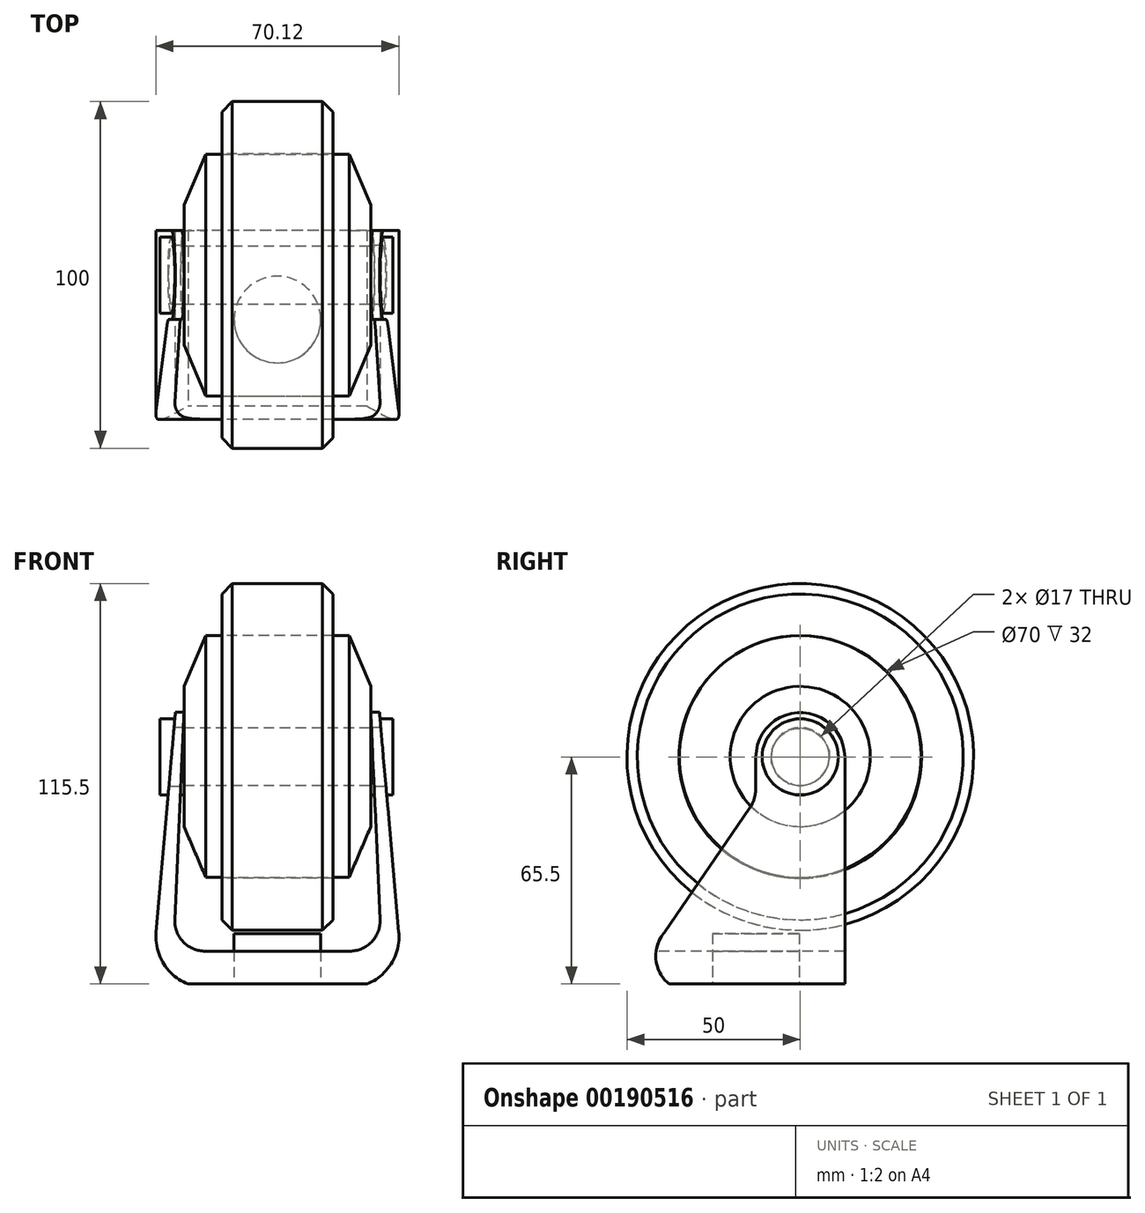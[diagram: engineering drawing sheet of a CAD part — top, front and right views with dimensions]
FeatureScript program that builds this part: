
annotation { "Feature Type Name" : "Feature", "Feature Type Description" : "" }
export const myFeature = defineFeature(function(context is Context, id is Id, definition is map)
    precondition{}
    {
        {
            var Q0;
            Q0=qCreatedBy(makeId("Top.planeOp"),FACE);
            var sketch = newSketch(context, id + "F0", { "sketchPlane" : qUnion([Q0])});
            skLineSegment(sketch, "E0.bottom", {"start": v(-35, 48) * mm, "end": v(35, 48) * mm});
            skLineSegment(sketch, "E0.top", {"start": v(-35, -48) * mm, "end": v(35, -48) * mm});
            skLineSegment(sketch, "E0.left", {"start": v(-35, 48) * mm, "end": v(-35, -48) * mm});
            skLineSegment(sketch, "E0.right", {"start": v(35, 48) * mm, "end": v(35, -48) * mm});
            skLineSegment(sketch, "E1", {"start": v(-35, 0) * mm, "end": v(35, 0) * mm, "construction": true});
            skLineSegment(sketch, "E2", {"start": v(0, 48) * mm, "end": v(0, -48) * mm, "construction": true});
            skLineSegment(sketch, "E3.bottom", {"start": v(-26.2, -41.35) * mm, "end": v(-17.8, -41.35) * mm});
            skLineSegment(sketch, "E3.top", {"start": v(-26.2, -31.65) * mm, "end": v(-17.8, -31.65) * mm});
            skLineSegment(sketch, "E3.left", {"start": v(-26.2, -41.35) * mm, "end": v(-26.2, -31.65) * mm});
            skLineSegment(sketch, "E3.right", {"start": v(-17.8, -41.35) * mm, "end": v(-17.8, -31.65) * mm});
            skPoint(sketch, "E4", {"position": v(-26.2, -36.5) * mm});
            skPoint(sketch, "E5", {"position": v(-22, -41.35) * mm});
            skLineSegment(sketch, "E6.MirrorCS", {"start": v(-26.2, 31.65) * mm, "end": v(-17.8, 31.65) * mm});
            skLineSegment(sketch, "E7.MirrorCS", {"start": v(-17.8, 41.35) * mm, "end": v(-17.8, 31.65) * mm});
            skPoint(sketch, "E8.MirrorP", {"position": v(-22, 41.35) * mm});
            skLineSegment(sketch, "E9.MirrorCS", {"start": v(-26.2, 41.35) * mm, "end": v(-17.8, 41.35) * mm});
            skLineSegment(sketch, "E10.MirrorCS", {"start": v(-26.2, 41.35) * mm, "end": v(-26.2, 31.65) * mm});
            skLineSegment(sketch, "E11.MirrorCS", {"start": v(17.8, 41.35) * mm, "end": v(17.8, 31.65) * mm});
            skLineSegment(sketch, "E12.MirrorCS", {"start": v(26.2, 31.65) * mm, "end": v(17.8, 31.65) * mm});
            skLineSegment(sketch, "E13.MirrorCS", {"start": v(26.2, 41.35) * mm, "end": v(26.2, 31.65) * mm});
            skLineSegment(sketch, "E14.MirrorCS", {"start": v(26.2, 41.35) * mm, "end": v(17.8, 41.35) * mm});
            skLineSegment(sketch, "E15.MirrorCS", {"start": v(26.2, -31.65) * mm, "end": v(17.8, -31.65) * mm});
            skLineSegment(sketch, "E16.MirrorCS", {"start": v(17.8, -41.35) * mm, "end": v(17.8, -31.65) * mm});
            skLineSegment(sketch, "E17.MirrorCS", {"start": v(26.2, -41.35) * mm, "end": v(17.8, -41.35) * mm});
            skLineSegment(sketch, "E18.MirrorCS", {"start": v(26.2, -41.35) * mm, "end": v(26.2, -31.65) * mm});
            skCircle(sketch, "E19", {"center": v(0, -41.35) * mm, "radius": 4.15 * mm});
            skCircle(sketch, "E20.MirrorC", {"center": v(0, 41.35) * mm, "radius": 4.15 * mm});
            skSolve(sketch);
        }
        {
            var Q0;
            Q0=makeQuery(id+"F0.imprint","IMPRINT",FACE,{"disambiguationData":[TD([[makeQuery(id+"F0.imprint","IMPRINT",EDGE,{"derivedFrom":sQuery(id+"F0.wireOp",EDGE,"E0.bottom")}),-1.0]])]});
            extrude(context, id + "F1", {"entities" : qUnion([Q0]), "depth" : 5 * mm});
        }
        {
            var Q0;
            Q0=qCreatedBy(makeId("Front.planeOp"),FACE);
            var sketch = newSketch(context, id + "F2", { "sketchPlane" : qUnion([Q0])});
            skLineSegment(sketch, "E21.0", {"start": v(-25, 5) * mm, "end": v(25, 5) * mm});
            skLineSegment(sketch, "E22.0.2", {"start": v(35, 5) * mm, "end": v(-35, 5) * mm, "construction": true});
            skLineSegment(sketch, "E23", {"start": v(0, 5) * mm, "end": v(0, 12) * mm});
            skLineSegment(sketch, "E24", {"start": v(0, 5) * mm, "end": v(-25, 5) * mm});
            skLineSegment(sketch, "E25", {"start": v(0, 12) * mm, "end": v(-25, 12) * mm});
            skArc(sketch, "E26", {"start": v(-25, 12) * mm, "mid": v(-25.8, 8.5) * mm, "end": v(-25, 5) * mm});
            skSolve(sketch);
        }
        {
            var Q0;
            Q0=makeQuery(id+"F2.imprint","IMPRINT",FACE,{"disambiguationData":[TD([[makeQuery(id+"F2.imprint","IMPRINT",EDGE,{"derivedFrom":sQuery(id+"F2.wireOp",EDGE,"E23")}),1.0]])]});
            var Q1;
            Q1=sQuery(id+"F2.wireOp",EDGE,"E23");
            revolve(context, id + "F3", {"operationType" : NewBodyOperationType.ADD, "entities" : qUnion([Q0]), "axis" : qUnion([Q1]), "revolveType" : RevolveType.FULL});
        }
        {
            var Q0;
            Q0=makeQuery(id+"F3.opRevolve","SWEPT_FACE",FACE,{"disambiguationData":[OSD([sQuery(id+"F2.wireOp",EDGE,"E25")])]});
            cPlane(context, id + "F4", {"entities" : qUnion([Q0]), "cplaneType" : CPlaneType.OFFSET, "offset" : 0 * mm, "width" : 150 * mm, "height" : 150 * mm});
        }
        {
            var Q0;
            Q0=qCreatedBy(id+"F4.planeOp",FACE);
            var sketch = newSketch(context, id + "F5", { "sketchPlane" : qUnion([Q0])});
            skCircle(sketch, "E27", {"center": v(0, 0) * mm, "radius": 12.5 * mm});
            skSolve(sketch);
        }
        {
            var Q0;
            Q0=makeQuery(id+"F5.imprint","IMPRINT",FACE,{"disambiguationData":[TD([[makeQuery(id+"F5.imprint","IMPRINT",EDGE,{"derivedFrom":sQuery(id+"F5.wireOp",EDGE,"E27")}),1.0]])]});
            extrude(context, id + "F6", {"entities" : qUnion([Q0]), "operationType" : NewBodyOperationType.ADD, "depth" : 15 * mm});
        }
        {
            var Q0;
            Q0=qCreatedBy(makeId("Front.planeOp"),FACE);
            cPlane(context, id + "F7", {"entities" : qUnion([Q0]), "cplaneType" : CPlaneType.OFFSET, "offset" : 27 * mm, "width" : 150 * mm, "height" : 150 * mm});
        }
        {
            var Q0;
            Q0=qCreatedBy(id+"F7.planeOp",FACE);
            var sketch = newSketch(context, id + "F8", { "sketchPlane" : qUnion([Q0])});
            skLineSegment(sketch, "E28", {"start": v(0, 12.5) * mm, "end": v(25.8, 12.5) * mm});
            skLineSegment(sketch, "E29", {"start": v(35, 27.44) * mm, "end": v(29.43, 90.85) * mm});
            skLineSegment(sketch, "E30", {"start": v(29.43, 90.85) * mm, "end": v(26.93, 90.85) * mm});
            skLineSegment(sketch, "E31", {"start": v(26.93, 90.85) * mm, "end": v(29.6, 31.09) * mm});
            skLineSegment(sketch, "E32", {"start": v(20.9, 22) * mm, "end": v(0, 22) * mm});
            skLineSegment(sketch, "E33", {"start": v(0, 0) * mm, "end": v(0, 60.5) * mm});
            skLineSegment(sketch, "E34.0", {"start": v(-12.5, 27) * mm, "end": v(28.78, 27) * mm, "construction": true});
            skPoint(sketch, "E35.orphan", {"position": v(12.5, 27) * mm});
            skPoint(sketch, "E36", {"position": v(25.8, 12.5) * mm});
            skPoint(sketch, "E37", {"position": v(31, 73) * mm});
            skPoint(sketch, "E38.visualSharp", {"position": v(30, 22) * mm});
            skLineSegment(sketch, "E39.MirrorCS", {"start": v(0, 12.5) * mm, "end": v(-25.8, 12.5) * mm});
            skLineSegment(sketch, "E40.MirrorCS", {"start": v(-20.9, 22) * mm, "end": v(0, 22) * mm});
            skLineSegment(sketch, "E41.MirrorCS", {"start": v(-26.93, 90.85) * mm, "end": v(-29.6, 31.09) * mm});
            skLineSegment(sketch, "E42.MirrorCS", {"start": v(-29.43, 90.85) * mm, "end": v(-26.93, 90.85) * mm});
            skLineSegment(sketch, "E43.MirrorCS", {"start": v(-35, 27.44) * mm, "end": v(-29.43, 90.85) * mm});
            skArc(sketch, "E44.MirrorCS", {"start": v(-35.04, 26.56) * mm, "mid": v(-35.03, 27) * mm, "end": v(-35, 27.44) * mm});
            skArc(sketch, "E45", {"start": v(35, 27.44) * mm, "mid": v(32.87, 18.45) * mm, "end": v(25.8, 12.5) * mm});
            skArc(sketch, "E46", {"start": v(29.6, 31.09) * mm, "mid": v(27.2, 24.69) * mm, "end": v(20.9, 22) * mm});
            skArc(sketch, "E47.MirrorCS", {"start": v(-29.6, 31.09) * mm, "mid": v(-27.2, 24.69) * mm, "end": v(-20.9, 22) * mm});
            skArc(sketch, "E48.MirrorCS", {"start": v(-35, 27.44) * mm, "mid": v(-32.87, 18.45) * mm, "end": v(-25.8, 12.5) * mm});
            skSolve(sketch);
        }
        {
            var Q0;
            Q0=qCreatedBy(makeId("Right.planeOp"),FACE);
            var sketch = newSketch(context, id + "F9", { "sketchPlane" : qUnion([Q0])});
            skLineSegment(sketch, "E49", {"start": v(-25, 12.5) * mm, "end": v(25.7, 12.5) * mm});
            skLineSegment(sketch, "E50", {"start": v(25.7, 12.5) * mm, "end": v(25.7, 78) * mm});
            skLineSegment(sketch, "E51", {"start": v(0, 78) * mm, "end": v(0, 68.86) * mm});
            skLineSegment(sketch, "E52", {"start": v(-1.76, 63.2) * mm, "end": v(-27, 26.5) * mm});
            skArc(sketch, "E53", {"start": v(25.7, 78) * mm, "mid": v(12.85, 90.85) * mm, "end": v(0, 78) * mm});
            skArc(sketch, "E54", {"start": v(-27, 26.5) * mm, "mid": v(-28.73, 19.1) * mm, "end": v(-25, 12.5) * mm});
            skCircle(sketch, "E55", {"center": v(12.85, 78) * mm, "radius": 8.5 * mm});
            skPoint(sketch, "E56.visualSharp", {"position": v(0, 65.75) * mm});
            skArc(sketch, "E56.filletArc", {"start": v(-1.76, 63.2) * mm, "mid": v(-0.45, 65.9) * mm, "end": v(0, 68.86) * mm});
            skSolve(sketch);
        }
        {
            var Q0;
            {var subQ1=sQuery(id+"F8.wireOp",EDGE,"E39.MirrorCS");Q0=makeQuery(id+"F8.imprint","IMPRINT",FACE,{"disambiguationData":[TD([[makeQuery(id+"F8.imprint","IMPRINT",EDGE,{"derivedFrom":subQ1}),-1.0]])]});}
            var Q1;
            {var subQ0=sQuery(id+"F8.wireOp",EDGE,"E28");Q1=makeQuery(id+"F8.imprint","IMPRINT",FACE,{"disambiguationData":[TD([[makeQuery(id+"F8.imprint","IMPRINT",EDGE,{"derivedFrom":subQ0}),1.0]])]});}
            extrude(context, id + "F10", {"entities" : qUnion([Q0, Q1]), "endBound" : BoundingType.SYMMETRIC, "oppositeDirection" : true, "depth" : 120 * mm});
        }
        {
            var Q0;
            Q0 = qSketchRegion(id + "F9", true);
            extrude(context, id + "F11", {"entities" : qUnion([Q0]), "operationType" : NewBodyOperationType.INTERSECT, "endBound" : BoundingType.SYMMETRIC, "depth" : 120 * mm});
        }
        {
            var Q0;
            Q0=makeQuery(id+"F1.opExtrude","SWEPT_BODY",BODY,{"disambiguationData":[OSD([sQuery(id+"F0.wireOp",EDGE,"E0.bottom"),sQuery(id+"F0.wireOp",EDGE,"E0.top"),sQuery(id+"F0.wireOp",EDGE,"E0.left"),sQuery(id+"F0.wireOp",EDGE,"E0.right"),sQuery(id+"F0.wireOp",EDGE,"E3.bottom"),sQuery(id+"F0.wireOp",EDGE,"E3.top"),sQuery(id+"F0.wireOp",EDGE,"E3.left"),sQuery(id+"F0.wireOp",EDGE,"E3.right"),sQuery(id+"F0.wireOp",EDGE,"E6.MirrorCS"),sQuery(id+"F0.wireOp",EDGE,"E7.MirrorCS"),sQuery(id+"F0.wireOp",EDGE,"E9.MirrorCS"),sQuery(id+"F0.wireOp",EDGE,"E10.MirrorCS"),sQuery(id+"F0.wireOp",EDGE,"E11.MirrorCS"),sQuery(id+"F0.wireOp",EDGE,"E12.MirrorCS"),sQuery(id+"F0.wireOp",EDGE,"E13.MirrorCS"),sQuery(id+"F0.wireOp",EDGE,"E14.MirrorCS"),sQuery(id+"F0.wireOp",EDGE,"E15.MirrorCS"),sQuery(id+"F0.wireOp",EDGE,"E16.MirrorCS"),sQuery(id+"F0.wireOp",EDGE,"E17.MirrorCS"),sQuery(id+"F0.wireOp",EDGE,"E18.MirrorCS"),sQuery(id+"F0.wireOp",EDGE,"E19"),sQuery(id+"F0.wireOp",EDGE,"E20.MirrorC")])]});
            var Q1;
            Q1=makeQuery(id+"F10.opExtrude","SWEPT_BODY",BODY,{"disambiguationData":[OSD([sQuery(id+"F8.wireOp",EDGE,"E28"),sQuery(id+"F8.wireOp",EDGE,"E29"),sQuery(id+"F8.wireOp",EDGE,"E30"),sQuery(id+"F8.wireOp",EDGE,"E31"),sQuery(id+"F8.wireOp",EDGE,"E32"),sQuery(id+"F8.wireOp",EDGE,"E39.MirrorCS"),sQuery(id+"F8.wireOp",EDGE,"E40.MirrorCS"),sQuery(id+"F8.wireOp",EDGE,"E41.MirrorCS"),sQuery(id+"F8.wireOp",EDGE,"E42.MirrorCS"),sQuery(id+"F8.wireOp",EDGE,"E43.MirrorCS"),sQuery(id+"F8.wireOp",EDGE,"E45"),sQuery(id+"F8.wireOp",EDGE,"E46"),sQuery(id+"F8.wireOp",EDGE,"E47.MirrorCS"),sQuery(id+"F8.wireOp",EDGE,"E48.MirrorCS")])]});
            booleanBodies(context, id + "F12", {"operationType" : BooleanOperationType.SUBTRACTION, "tools" : qUnion([Q0]), "targets" : qUnion([Q1]), "keepTools" : true});
        }
        {
            var Q0;
            Q0=qCreatedBy(makeId("Right.planeOp"),FACE);
            var sketch = newSketch(context, id + "F13", { "sketchPlane" : qUnion([Q0])});
            skCircle(sketch, "E57.0", {"center": v(12.85, 78) * mm, "radius": 8.5 * mm});
            skCircle(sketch, "E58", {"center": v(12.85, 78) * mm, "radius": 50 * mm});
            skCircle(sketch, "E59", {"center": v(12.85, 78) * mm, "radius": 35 * mm});
            skCircle(sketch, "E60", {"center": v(12.85, 78) * mm, "radius": 25 * mm});
            skSolve(sketch);
        }
        {
            var Q0;
            Q0=makeQuery(id+"F13.imprint","IMPRINT",FACE,{"disambiguationData":[TD([[makeQuery(id+"F13.imprint","IMPRINT",EDGE,{"derivedFrom":sQuery(id+"F13.wireOp",EDGE,"E58")}),1.0]])]});
            extrude(context, id + "F14", {"entities" : qUnion([Q0]), "endBound" : BoundingType.SYMMETRIC, "depth" : 32 * mm});
        }
        {
            var Q0;
            Q0=makeQuery(id+"F14.opExtrude","CAP_EDGE",EDGE,{"disambiguationData":[OSD([sQuery(id+"F13.wireOp",EDGE,"E58")])],"isStart":false});
            var Q1;
            Q1=makeQuery(id+"F14.opExtrude","CAP_EDGE",EDGE,{"disambiguationData":[OSD([sQuery(id+"F13.wireOp",EDGE,"E58")])],"isStart":true});
            chamfer(context, id + "F15", {"entities" : qUnion([Q0, Q1]), "width" : 3 * mm, "tangentPropagation" : true});
        }
        {
            var Q0;
            Q0=qCreatedBy(makeId("Front.planeOp"),FACE);
            var Q1;
            Q1=sQuery(id+"F13.wireOp",VERTEX,"E57.0.center");
            cPlane(context, id + "F16", {"entities" : qUnion([Q0, Q1]), "cplaneType" : CPlaneType.PLANE_POINT, "offset" : 25 * mm, "width" : 150 * mm, "height" : 150 * mm});
        }
        {
            var Q0;
            Q0=qCreatedBy(id+"F16.planeOp",FACE);
            var sketch = newSketch(context, id + "F17", { "sketchPlane" : qUnion([Q0])});
            skLineSegment(sketch, "E61.0", {"start": v(-16, 113) * mm, "end": v(-16, 43) * mm, "construction": true});
            skLineSegment(sketch, "E62.0", {"start": v(16, 113) * mm, "end": v(16, 43) * mm, "construction": true});
            skLineSegment(sketch, "E63", {"start": v(0, 113) * mm, "end": v(-16, 113) * mm});
            skLineSegment(sketch, "E64", {"start": v(-16, 113) * mm, "end": v(-20.67, 113) * mm});
            skLineSegment(sketch, "E65", {"start": v(-20.67, 113) * mm, "end": v(-26.93, 98.35) * mm});
            skLineSegment(sketch, "E66", {"start": v(-26.93, 98.35) * mm, "end": v(-26.93, 78.14) * mm});
            skLineSegment(sketch, "E67", {"start": v(0, 78.14) * mm, "end": v(0, 113) * mm});
            skLineSegment(sketch, "E68.MirrorCS", {"start": v(26.93, 98.35) * mm, "end": v(26.93, 78.14) * mm});
            skLineSegment(sketch, "E69.MirrorCS", {"start": v(20.67, 113) * mm, "end": v(26.93, 98.35) * mm});
            skLineSegment(sketch, "E70.MirrorCS", {"start": v(16, 113) * mm, "end": v(20.67, 113) * mm});
            skLineSegment(sketch, "E71.MirrorCS", {"start": v(0, 113) * mm, "end": v(16, 113) * mm});
            skPoint(sketch, "E72.MirrorCS.end.orphan", {"position": v(-26.93, 78.14) * mm});
            skPoint(sketch, "E73.MirrorCS.end.orphan", {"position": v(26.93, 78.14) * mm});
            skLineSegment(sketch, "E74", {"start": v(-29.81, 86.5) * mm, "end": v(-27.13, 86.5) * mm, "construction": true});
            skLineSegment(sketch, "E75", {"start": v(-27.88, 69.5) * mm, "end": v(-31.3, 69.5) * mm, "construction": true});
            skLineSegment(sketch, "E76", {"start": v(-27.13, 86.5) * mm, "end": v(26.93, 86.5) * mm});
            skLineSegment(sketch, "E77", {"start": v(0, 78.14) * mm, "end": v(-26.93, 78.14) * mm, "construction": true});
            skSolve(sketch);
        }
        {
            var Q0;
            Q0=makeQuery(id+"F17.imprint","IMPRINT",FACE,{"disambiguationData":[TD([[makeQuery(id+"F17.imprint","IMPRINT",EDGE,{"derivedFrom":sQuery(id+"F17.wireOp",EDGE,"E63")}),1.0]])]});
            var Q1;
            Q1=makeQuery(id+"F17.imprint","IMPRINT",FACE,{"disambiguationData":[TD([[makeQuery(id+"F17.imprint","IMPRINT",EDGE,{"derivedFrom":sQuery(id+"F17.wireOp",EDGE,"E67")}),-1.0]])]});
            var Q2;
            Q2=sQuery(id+"F17.wireOp",EDGE,"E77");
            revolve(context, id + "F18", {"entities" : qUnion([Q0, Q1]), "axis" : qUnion([Q2]), "revolveType" : RevolveType.FULL});
        }
        {
            var Q0;
            Q0=makeQuery(id+"F18.opRevolve","SWEPT_FACE",FACE,{"disambiguationData":[OSD([sQuery(id+"F17.wireOp",EDGE,"E66")])]});
            cPlane(context, id + "F19", {"entities" : qUnion([Q0]), "cplaneType" : CPlaneType.OFFSET, "offset" : 7 * mm, "width" : 150 * mm, "height" : 150 * mm});
        }
        {
            var Q0;
            Q0=qCreatedBy(id+"F19.planeOp",FACE);
            var sketch = newSketch(context, id + "F20", { "sketchPlane" : qUnion([Q0])});
            skCircle(sketch, "E78.0", {"center": v(-12.85, 78) * mm, "radius": 8.5 * mm, "construction": true});
            skCircle(sketch, "E79", {"center": v(-12.85, 78) * mm, "radius": 11 * mm});
            skSolve(sketch);
        }
        {
            var Q0;
            Q0 = qSketchRegion(id + "F20", true);
            extrude(context, id + "F21", {"entities" : qUnion([Q0]), "oppositeDirection" : true, "depth" : 67.2 * mm});
        }
        {
            var Q0;
            Q0=makeQuery(id+"F18.opRevolve","SWEPT_BODY",BODY,{"disambiguationData":[OSD([sQuery(id+"F17.wireOp",EDGE,"E63"),sQuery(id+"F17.wireOp",EDGE,"E64"),sQuery(id+"F17.wireOp",EDGE,"E65"),sQuery(id+"F17.wireOp",EDGE,"E66"),sQuery(id+"F17.wireOp",EDGE,"E68.MirrorCS"),sQuery(id+"F17.wireOp",EDGE,"E69.MirrorCS"),sQuery(id+"F17.wireOp",EDGE,"E70.MirrorCS"),sQuery(id+"F17.wireOp",EDGE,"E71.MirrorCS"),sQuery(id+"F17.wireOp",EDGE,"E76")])]});
            var Q1;
            Q1=makeQuery(id+"F10.opExtrude","SWEPT_BODY",BODY,{"disambiguationData":[OSD([sQuery(id+"F8.wireOp",EDGE,"E28"),sQuery(id+"F8.wireOp",EDGE,"E29"),sQuery(id+"F8.wireOp",EDGE,"E30"),sQuery(id+"F8.wireOp",EDGE,"E31"),sQuery(id+"F8.wireOp",EDGE,"E32"),sQuery(id+"F8.wireOp",EDGE,"E39.MirrorCS"),sQuery(id+"F8.wireOp",EDGE,"E40.MirrorCS"),sQuery(id+"F8.wireOp",EDGE,"E41.MirrorCS"),sQuery(id+"F8.wireOp",EDGE,"E42.MirrorCS"),sQuery(id+"F8.wireOp",EDGE,"E43.MirrorCS"),sQuery(id+"F8.wireOp",EDGE,"E45"),sQuery(id+"F8.wireOp",EDGE,"E46"),sQuery(id+"F8.wireOp",EDGE,"E47.MirrorCS"),sQuery(id+"F8.wireOp",EDGE,"E48.MirrorCS")])]});
            var Q2;
            Q2=makeQuery(id+"F21.opExtrude","SWEPT_BODY",BODY,{"disambiguationData":[OSD([sQuery(id+"F20.wireOp",EDGE,"E79")])]});
            booleanBodies(context, id + "F22", {"operationType" : BooleanOperationType.SUBTRACTION, "tools" : qUnion([Q0, Q1]), "targets" : qUnion([Q2]), "keepTools" : true});
        }
    });
